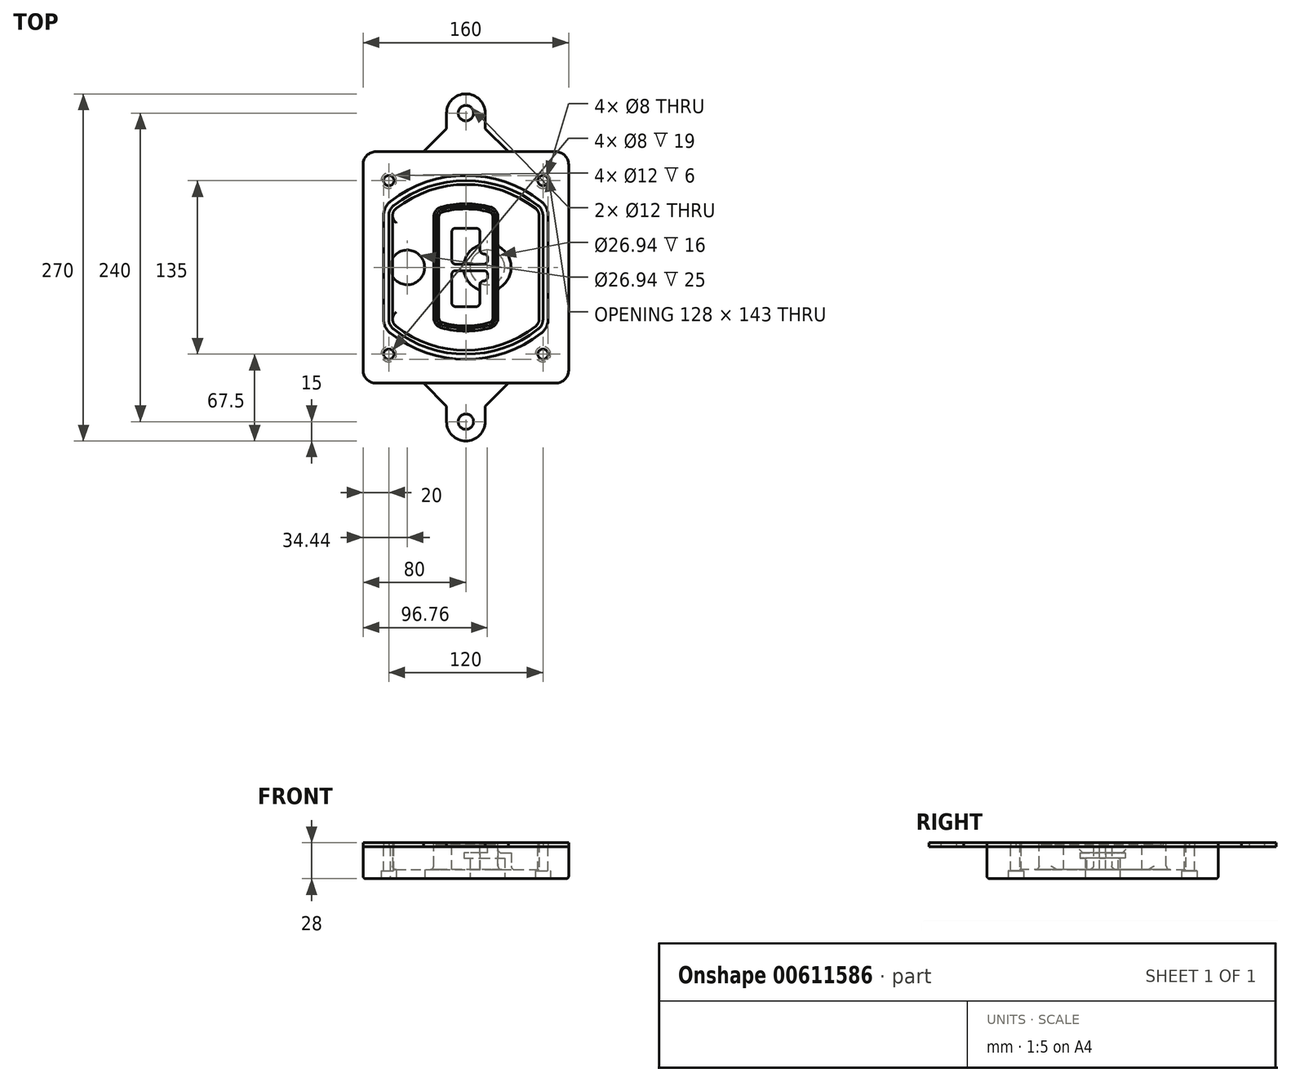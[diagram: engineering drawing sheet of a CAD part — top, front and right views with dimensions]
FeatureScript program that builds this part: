
annotation { "Feature Type Name" : "Feature", "Feature Type Description" : "" }
export const myFeature = defineFeature(function(context is Context, id is Id, definition is map)
    precondition{}
    {
        {
            var Q0;
            Q0=qCreatedBy(makeId("Top.planeOp"),FACE);
            var sketch = newSketch(context, id + "F0", { "sketchPlane" : qUnion([Q0])});
            skPoint(sketch, "E0.rect.middle", {"position": v(0, 0) * mm});
            skLineSegment(sketch, "E1.bottom", {"start": v(-70, -90) * mm, "end": v(70, -90) * mm});
            skLineSegment(sketch, "E1.top", {"start": v(-70, 90) * mm, "end": v(70, 90) * mm});
            skLineSegment(sketch, "E1.left", {"start": v(-80, -80) * mm, "end": v(-80, 80) * mm});
            skLineSegment(sketch, "E1.right", {"start": v(80, -80) * mm, "end": v(80, 80) * mm});
            skLineSegment(sketch, "E2", {"start": v(-80, 90) * mm, "end": v(80, -90) * mm, "construction": true});
            skLineSegment(sketch, "E3", {"start": v(80, 90) * mm, "end": v(-80, -90) * mm, "construction": true});
            skCircle(sketch, "E4", {"center": v(-60, 67.5) * mm, "radius": 4 * mm});
            skCircle(sketch, "E5", {"center": v(60, 67.5) * mm, "radius": 4 * mm});
            skCircle(sketch, "E6", {"center": v(60, -67.5) * mm, "radius": 4 * mm});
            skCircle(sketch, "E7", {"center": v(-60, -67.5) * mm, "radius": 4 * mm});
            skLineSegment(sketch, "E8", {"start": v(-60, 67.5) * mm, "end": v(60, 67.5) * mm, "construction": true});
            skLineSegment(sketch, "E9", {"start": v(60, 67.5) * mm, "end": v(60, -67.5) * mm, "construction": true});
            skLineSegment(sketch, "E10", {"start": v(60, -67.5) * mm, "end": v(-60, -67.5) * mm, "construction": true});
            skLineSegment(sketch, "E11", {"start": v(-60, -67.5) * mm, "end": v(-60, 67.5) * mm, "construction": true});
            skLineSegment(sketch, "E12", {"start": v(-60, 40.3) * mm, "end": v(-60, -40.3) * mm});
            skLineSegment(sketch, "E13", {"start": v(60, 40.3) * mm, "end": v(60, -40.3) * mm});
            skArc(sketch, "E14", {"start": v(56.15, 48.18) * mm, "mid": v(0, 67.5) * mm, "end": v(-56.15, 48.18) * mm});
            skArc(sketch, "E15", {"start": v(-56.15, -48.18) * mm, "mid": v(0, -67.5) * mm, "end": v(56.15, -48.18) * mm});
            skLineSegment(sketch, "E16", {"start": v(-60, 0) * mm, "end": v(60, 0) * mm, "construction": true});
            skPoint(sketch, "E17.visualSharp", {"position": v(-60, -45) * mm});
            skArc(sketch, "E17.filletArc", {"start": v(-60, -40.3) * mm, "mid": v(-58.99, -44.68) * mm, "end": v(-56.15, -48.18) * mm});
            skPoint(sketch, "E18.visualSharp", {"position": v(-60, 45) * mm});
            skArc(sketch, "E18.filletArc", {"start": v(-56.15, 48.18) * mm, "mid": v(-58.99, 44.68) * mm, "end": v(-60, 40.3) * mm});
            skPoint(sketch, "E19.visualSharp", {"position": v(60, 45) * mm});
            skArc(sketch, "E19.filletArc", {"start": v(60, 40.3) * mm, "mid": v(58.99, 44.68) * mm, "end": v(56.15, 48.18) * mm});
            skPoint(sketch, "E20.visualSharp", {"position": v(60, -45) * mm});
            skArc(sketch, "E20.filletArc", {"start": v(56.15, -48.18) * mm, "mid": v(58.99, -44.68) * mm, "end": v(60, -40.3) * mm});
            skPoint(sketch, "E21.visualSharp", {"position": v(-80, 90) * mm});
            skArc(sketch, "E21.filletArc", {"start": v(-70, 90) * mm, "mid": v(-77.07, 87.07) * mm, "end": v(-80, 80) * mm});
            skPoint(sketch, "E22.visualSharp", {"position": v(80, 90) * mm});
            skArc(sketch, "E22.filletArc", {"start": v(80, 80) * mm, "mid": v(77.07, 87.07) * mm, "end": v(70, 90) * mm});
            skPoint(sketch, "E23.visualSharp", {"position": v(80, -90) * mm});
            skArc(sketch, "E23.filletArc", {"start": v(70, -90) * mm, "mid": v(77.07, -87.07) * mm, "end": v(80, -80) * mm});
            skPoint(sketch, "E24.visualSharp", {"position": v(-80, -90) * mm});
            skArc(sketch, "E24.filletArc", {"start": v(-80, -80) * mm, "mid": v(-77.07, -87.07) * mm, "end": v(-70, -90) * mm});
            skArc(sketch, "E25.0", {"start": v(57, 40.3) * mm, "mid": v(56.3, 43.36) * mm, "end": v(54.3, 45.81) * mm});
            skLineSegment(sketch, "E25.1", {"start": v(57, 40.3) * mm, "end": v(57, -40.3) * mm});
            skArc(sketch, "E25.2", {"start": v(54.3, -45.81) * mm, "mid": v(56.3, -43.36) * mm, "end": v(57, -40.3) * mm});
            skArc(sketch, "E25.3", {"start": v(-54.3, -45.81) * mm, "mid": v(0, -64.5) * mm, "end": v(54.3, -45.81) * mm});
            skArc(sketch, "E25.4", {"start": v(-57, -40.3) * mm, "mid": v(-56.3, -43.36) * mm, "end": v(-54.3, -45.81) * mm});
            skArc(sketch, "E25.5", {"start": v(54.3, 45.81) * mm, "mid": v(0, 64.5) * mm, "end": v(-54.3, 45.81) * mm});
            skLineSegment(sketch, "E25.6", {"start": v(-57, 40.3) * mm, "end": v(-57, -40.3) * mm});
            skArc(sketch, "E25.7", {"start": v(-54.3, 45.81) * mm, "mid": v(-56.3, 43.36) * mm, "end": v(-57, 40.3) * mm});
            skArc(sketch, "E26.0", {"start": v(-58.62, 51.33) * mm, "mid": v(-62.58, 46.43) * mm, "end": v(-64, 40.3) * mm});
            skArc(sketch, "E26.1", {"start": v(58.62, 51.33) * mm, "mid": v(0, 71.5) * mm, "end": v(-58.62, 51.33) * mm});
            skArc(sketch, "E26.2", {"start": v(64, 40.3) * mm, "mid": v(62.58, 46.43) * mm, "end": v(58.62, 51.33) * mm});
            skLineSegment(sketch, "E26.3", {"start": v(64, 40.3) * mm, "end": v(64, -40.3) * mm});
            skArc(sketch, "E26.4", {"start": v(58.62, -51.33) * mm, "mid": v(62.58, -46.43) * mm, "end": v(64, -40.3) * mm});
            skLineSegment(sketch, "E26.5", {"start": v(-64, 40.3) * mm, "end": v(-64, -40.3) * mm});
            skArc(sketch, "E26.6", {"start": v(-58.62, -51.33) * mm, "mid": v(0, -71.5) * mm, "end": v(58.62, -51.33) * mm});
            skArc(sketch, "E26.7", {"start": v(-64, -40.3) * mm, "mid": v(-62.58, -46.43) * mm, "end": v(-58.62, -51.33) * mm});
            skSolve(sketch);
        }
        {
            var Q0;
            Q0=makeQuery(id+"F0.imprint","IMPRINT",FACE,{"disambiguationData":[TD([[makeQuery(id+"F0.imprint","IMPRINT",EDGE,{"derivedFrom":sQuery(id+"F0.wireOp",EDGE,"E1.bottom")}),1.0]])]});
            var Q1;
            Q1=makeQuery(id+"F0.imprint","IMPRINT",FACE,{"disambiguationData":[TD([[makeQuery(id+"F0.imprint","IMPRINT",EDGE,{"derivedFrom":sQuery(id+"F0.wireOp",EDGE,"E12")}),1.0]])]});
            var Q2;
            Q2=makeQuery(id+"F0.imprint","IMPRINT",FACE,{"disambiguationData":[TD([[makeQuery(id+"F0.imprint","IMPRINT",EDGE,{"derivedFrom":sQuery(id+"F0.wireOp",EDGE,"E25.0")}),1.0]])]});
            var Q3;
            Q3=makeQuery(id+"F0.imprint","IMPRINT",FACE,{"disambiguationData":[TD([[makeQuery(id+"F0.imprint","IMPRINT",EDGE,{"derivedFrom":sQuery(id+"F0.wireOp",EDGE,"E12")}),-1.0]])]});
            extrude(context, id + "F1", {"entities" : qUnion([Q0, Q1, Q2, Q3]), "oppositeDirection" : true, "depth" : 25 * mm});
        }
        {
            var Q0;
            Q0=makeQuery(id+"F0.imprint","IMPRINT",FACE,{"disambiguationData":[TD([[makeQuery(id+"F0.imprint","IMPRINT",EDGE,{"derivedFrom":sQuery(id+"F0.wireOp",EDGE,"E12")}),1.0]])]});
            extrude(context, id + "F2", {"entities" : qUnion([Q0]), "operationType" : NewBodyOperationType.ADD, "depth" : 3 * mm});
        }
        {
            var Q0;
            Q0=makeQuery(id+"F0.imprint","IMPRINT",FACE,{"disambiguationData":[TD([[makeQuery(id+"F0.imprint","IMPRINT",EDGE,{"derivedFrom":sQuery(id+"F0.wireOp",EDGE,"E25.0")}),1.0]])]});
            extrude(context, id + "F3", {"entities" : qUnion([Q0]), "operationType" : NewBodyOperationType.REMOVE, "oppositeDirection" : true, "depth" : 18 * mm});
        }
        {
            var Q0;
            Q0=makeQuery(id+"F2.opExtrude","CAP_FACE",FACE,{"disambiguationData":[OSD([sQuery(id+"F0.wireOp",EDGE,"E12"),sQuery(id+"F0.wireOp",EDGE,"E13"),sQuery(id+"F0.wireOp",EDGE,"E14"),sQuery(id+"F0.wireOp",EDGE,"E15"),sQuery(id+"F0.wireOp",EDGE,"E17.filletArc"),sQuery(id+"F0.wireOp",EDGE,"E18.filletArc"),sQuery(id+"F0.wireOp",EDGE,"E19.filletArc"),sQuery(id+"F0.wireOp",EDGE,"E20.filletArc"),sQuery(id+"F0.wireOp",EDGE,"E25.0"),sQuery(id+"F0.wireOp",EDGE,"E25.1"),sQuery(id+"F0.wireOp",EDGE,"E25.2"),sQuery(id+"F0.wireOp",EDGE,"E25.3"),sQuery(id+"F0.wireOp",EDGE,"E25.4"),sQuery(id+"F0.wireOp",EDGE,"E25.5"),sQuery(id+"F0.wireOp",EDGE,"E25.6"),sQuery(id+"F0.wireOp",EDGE,"E25.7")])],"isStart":false});
            var sketch = newSketch(context, id + "F4", { "sketchPlane" : qUnion([Q0])});
            skArc(sketch, "E27.0", {"start": v(-19.08, -46.97) * mm, "mid": v(0, -49.5) * mm, "end": v(19.08, -46.97) * mm});
            skArc(sketch, "E28.0", {"start": v(19.08, 46.97) * mm, "mid": v(0, 49.5) * mm, "end": v(-19.08, 46.97) * mm});
            skLineSegment(sketch, "E29", {"start": v(-25, 39.25) * mm, "end": v(-25, -39.25) * mm});
            skLineSegment(sketch, "E30", {"start": v(25, 39.25) * mm, "end": v(25, -39.25) * mm});
            skLineSegment(sketch, "E31", {"start": v(-25, 45.1) * mm, "end": v(25, 45.1) * mm, "construction": true});
            skLineSegment(sketch, "E32", {"start": v(-25, -45.1) * mm, "end": v(25, -45.1) * mm, "construction": true});
            skPoint(sketch, "E33.visualSharp", {"position": v(-25, 45.1) * mm});
            skArc(sketch, "E33.filletArc", {"start": v(-19.08, 46.97) * mm, "mid": v(-23.35, 44.11) * mm, "end": v(-25, 39.25) * mm});
            skPoint(sketch, "E34.visualSharp", {"position": v(25, 45.1) * mm});
            skArc(sketch, "E34.filletArc", {"start": v(25, 39.25) * mm, "mid": v(23.35, 44.11) * mm, "end": v(19.08, 46.97) * mm});
            skPoint(sketch, "E35.visualSharp", {"position": v(25, -45.1) * mm});
            skArc(sketch, "E35.filletArc", {"start": v(19.08, -46.97) * mm, "mid": v(23.35, -44.11) * mm, "end": v(25, -39.25) * mm});
            skPoint(sketch, "E36.visualSharp", {"position": v(-25, -45.1) * mm});
            skArc(sketch, "E36.filletArc", {"start": v(-25, -39.25) * mm, "mid": v(-23.35, -44.11) * mm, "end": v(-19.08, -46.97) * mm});
            skArc(sketch, "E37.0", {"start": v(54.3, 45.81) * mm, "mid": v(0, 64.5) * mm, "end": v(-54.3, 45.81) * mm});
            skArc(sketch, "E37.1", {"start": v(-54.3, 45.81) * mm, "mid": v(-56.3, 43.36) * mm, "end": v(-57, 40.3) * mm});
            skLineSegment(sketch, "E37.2", {"start": v(-57, 40.3) * mm, "end": v(-57, -40.3) * mm});
            skArc(sketch, "E37.3", {"start": v(-57, -40.3) * mm, "mid": v(-56.3, -43.36) * mm, "end": v(-54.3, -45.81) * mm});
            skArc(sketch, "E37.4", {"start": v(-54.3, -45.81) * mm, "mid": v(0, -64.5) * mm, "end": v(54.3, -45.81) * mm});
            skArc(sketch, "E37.5", {"start": v(54.3, -45.81) * mm, "mid": v(56.3, -43.36) * mm, "end": v(57, -40.3) * mm});
            skLineSegment(sketch, "E37.6", {"start": v(57, 40.3) * mm, "end": v(57, -40.3) * mm});
            skArc(sketch, "E37.7", {"start": v(57, 40.3) * mm, "mid": v(56.3, 43.36) * mm, "end": v(54.3, 45.81) * mm});
            skLineSegment(sketch, "E38.0", {"start": v(23, 39.25) * mm, "end": v(23, -39.25) * mm});
            skArc(sketch, "E38.1", {"start": v(18.56, -45.04) * mm, "mid": v(21.76, -42.9) * mm, "end": v(23, -39.25) * mm});
            skArc(sketch, "E38.2", {"start": v(-18.56, -45.04) * mm, "mid": v(0, -47.5) * mm, "end": v(18.56, -45.04) * mm});
            skArc(sketch, "E38.3", {"start": v(-23, -39.25) * mm, "mid": v(-21.76, -42.9) * mm, "end": v(-18.56, -45.04) * mm});
            skLineSegment(sketch, "E38.4", {"start": v(-23, 39.25) * mm, "end": v(-23, -39.25) * mm});
            skArc(sketch, "E38.5", {"start": v(23, 39.25) * mm, "mid": v(21.76, 42.9) * mm, "end": v(18.56, 45.04) * mm});
            skArc(sketch, "E38.6", {"start": v(-18.56, 45.04) * mm, "mid": v(-21.76, 42.9) * mm, "end": v(-23, 39.25) * mm});
            skArc(sketch, "E38.7", {"start": v(18.56, 45.04) * mm, "mid": v(0, 47.5) * mm, "end": v(-18.56, 45.04) * mm});
            skArc(sketch, "E39.0", {"start": v(21, 39.25) * mm, "mid": v(20.18, 41.68) * mm, "end": v(18.04, 43.1) * mm});
            skLineSegment(sketch, "E39.1", {"start": v(21, 39.25) * mm, "end": v(21, -39.25) * mm});
            skArc(sketch, "E39.2", {"start": v(18.04, -43.1) * mm, "mid": v(20.18, -41.68) * mm, "end": v(21, -39.25) * mm});
            skArc(sketch, "E39.3", {"start": v(-18.04, -43.1) * mm, "mid": v(0, -45.5) * mm, "end": v(18.04, -43.1) * mm});
            skArc(sketch, "E39.4", {"start": v(-21, -39.25) * mm, "mid": v(-20.18, -41.68) * mm, "end": v(-18.04, -43.1) * mm});
            skArc(sketch, "E39.5", {"start": v(18.04, 43.1) * mm, "mid": v(0, 45.5) * mm, "end": v(-18.04, 43.1) * mm});
            skLineSegment(sketch, "E39.6", {"start": v(-21, 39.25) * mm, "end": v(-21, -39.25) * mm});
            skArc(sketch, "E39.7", {"start": v(-18.04, 43.1) * mm, "mid": v(-20.18, 41.68) * mm, "end": v(-21, 39.25) * mm});
            skLineSegment(sketch, "E40", {"start": v(-25, 0) * mm, "end": v(25, 0) * mm, "construction": true});
            skLineSegment(sketch, "E41", {"start": v(-11, 5.5) * mm, "end": v(-11, 27.5) * mm});
            skLineSegment(sketch, "E42", {"start": v(-8, 30.5) * mm, "end": v(8, 30.5) * mm});
            skLineSegment(sketch, "E43", {"start": v(11, 27.5) * mm, "end": v(11, 13.5) * mm});
            skLineSegment(sketch, "E44", {"start": v(14, 10.5) * mm, "end": v(14, 10.5) * mm});
            skLineSegment(sketch, "E45", {"start": v(17, 7.5) * mm, "end": v(17, 5.5) * mm});
            skLineSegment(sketch, "E46", {"start": v(14, 2.5) * mm, "end": v(-8, 2.5) * mm});
            skPoint(sketch, "E47.visualSharp", {"position": v(-11, 30.5) * mm});
            skArc(sketch, "E47.filletArc", {"start": v(-8, 30.5) * mm, "mid": v(-10.12, 29.62) * mm, "end": v(-11, 27.5) * mm});
            skPoint(sketch, "E48.visualSharp", {"position": v(11, 30.5) * mm});
            skArc(sketch, "E48.filletArc", {"start": v(11, 27.5) * mm, "mid": v(10.12, 29.62) * mm, "end": v(8, 30.5) * mm});
            skPoint(sketch, "E49.visualSharp", {"position": v(11, 10.5) * mm});
            skArc(sketch, "E49.filletArc", {"start": v(11, 13.5) * mm, "mid": v(11.88, 11.38) * mm, "end": v(14, 10.5) * mm});
            skPoint(sketch, "E50.visualSharp", {"position": v(17, 10.5) * mm});
            skArc(sketch, "E50.filletArc", {"start": v(17, 7.5) * mm, "mid": v(16.12, 9.62) * mm, "end": v(14, 10.5) * mm});
            skPoint(sketch, "E51.visualSharp", {"position": v(17, 2.5) * mm});
            skArc(sketch, "E51.filletArc", {"start": v(14, 2.5) * mm, "mid": v(16.12, 3.38) * mm, "end": v(17, 5.5) * mm});
            skPoint(sketch, "E52.visualSharp", {"position": v(-11, 2.5) * mm});
            skArc(sketch, "E52.filletArc", {"start": v(-11, 5.5) * mm, "mid": v(-10.12, 3.38) * mm, "end": v(-8, 2.5) * mm});
            skLineSegment(sketch, "E53.0.MirrorCS", {"start": v(14, -2.5) * mm, "end": v(-8, -2.5) * mm});
            skArc(sketch, "E54.0.MirrorCS", {"start": v(-11, -5.5) * mm, "mid": v(-10.12, -3.38) * mm, "end": v(-8, -2.5) * mm});
            skLineSegment(sketch, "E55.0.MirrorCS", {"start": v(-11, -5.5) * mm, "end": v(-11, -27.5) * mm});
            skArc(sketch, "E56.0.MirrorCS", {"start": v(-8, -30.5) * mm, "mid": v(-10.12, -29.62) * mm, "end": v(-11, -27.5) * mm});
            skLineSegment(sketch, "E57.0.MirrorCS", {"start": v(-8, -30.5) * mm, "end": v(8, -30.5) * mm});
            skArc(sketch, "E58.0.MirrorCS", {"start": v(11, -27.5) * mm, "mid": v(10.12, -29.62) * mm, "end": v(8, -30.5) * mm});
            skLineSegment(sketch, "E59.0.MirrorCS", {"start": v(11, -27.5) * mm, "end": v(11, -13.5) * mm});
            skArc(sketch, "E60.0.MirrorCS", {"start": v(11, -13.5) * mm, "mid": v(11.88, -11.38) * mm, "end": v(14, -10.5) * mm});
            skArc(sketch, "E61.0.MirrorCS", {"start": v(17, -7.5) * mm, "mid": v(16.12, -9.62) * mm, "end": v(14, -10.5) * mm});
            skLineSegment(sketch, "E62.0.MirrorCS", {"start": v(17, -7.5) * mm, "end": v(17, -5.5) * mm});
            skArc(sketch, "E63.0.MirrorCS", {"start": v(14, -2.5) * mm, "mid": v(16.12, -3.38) * mm, "end": v(17, -5.5) * mm});
            skSolve(sketch);
        }
        {
            var Q0;
            Q0=makeQuery(id+"F4.imprint","IMPRINT",FACE,{"disambiguationData":[TD([[makeQuery(id+"F4.imprint","IMPRINT",EDGE,{"derivedFrom":sQuery(id+"F4.wireOp",EDGE,"E27.0")}),1.0]])]});
            var Q1;
            Q1=makeQuery(id+"F4.imprint","IMPRINT",FACE,{"disambiguationData":[TD([[makeQuery(id+"F4.imprint","IMPRINT",EDGE,{"derivedFrom":sQuery(id+"F4.wireOp",EDGE,"E38.0")}),-1.0]])]});
            var Q2;
            Q2=makeQuery(id+"F4.imprint","IMPRINT",FACE,{"disambiguationData":[TD([[makeQuery(id+"F4.imprint","IMPRINT",EDGE,{"derivedFrom":sQuery(id+"F4.wireOp",EDGE,"E39.0")}),1.0]])]});
            extrude(context, id + "F5", {"entities" : qUnion([Q0, Q1, Q2]), "operationType" : NewBodyOperationType.ADD, "endBound" : BoundingType.UP_TO_NEXT, "oppositeDirection" : true, "depth" : 25 * mm});
        }
        {
            var Q0;
            Q0=makeQuery(id+"F4.imprint","IMPRINT",FACE,{"disambiguationData":[TD([[makeQuery(id+"F4.imprint","IMPRINT",EDGE,{"derivedFrom":sQuery(id+"F4.wireOp",EDGE,"E38.0")}),-1.0]])]});
            extrude(context, id + "F6", {"entities" : qUnion([Q0]), "operationType" : NewBodyOperationType.REMOVE, "oppositeDirection" : true, "depth" : 2 * mm});
        }
        {
            var Q0;
            Q0=makeQuery(id+"F1.opExtrude","CAP_FACE",FACE,{"disambiguationData":[OSD([sQuery(id+"F0.wireOp",EDGE,"E1.bottom"),sQuery(id+"F0.wireOp",EDGE,"E1.top"),sQuery(id+"F0.wireOp",EDGE,"E1.left"),sQuery(id+"F0.wireOp",EDGE,"E1.right"),sQuery(id+"F0.wireOp",EDGE,"E4"),sQuery(id+"F0.wireOp",EDGE,"E5"),sQuery(id+"F0.wireOp",EDGE,"E6"),sQuery(id+"F0.wireOp",EDGE,"E7"),sQuery(id+"F0.wireOp",EDGE,"E21.filletArc"),sQuery(id+"F0.wireOp",EDGE,"E22.filletArc"),sQuery(id+"F0.wireOp",EDGE,"E23.filletArc"),sQuery(id+"F0.wireOp",EDGE,"E24.filletArc")])],"isStart":false});
            var sketch = newSketch(context, id + "F7", { "sketchPlane" : qUnion([Q0])});
            skCircle(sketch, "E64", {"center": v(16.76, 0) * mm, "radius": 13.47 * mm});
            skCircle(sketch, "E65", {"center": v(-45.56, 0) * mm, "radius": 13.47 * mm});
            skLineSegment(sketch, "E66", {"start": v(80, 0) * mm, "end": v(-80, 0) * mm});
            skCircle(sketch, "E67", {"center": v(16.76, 0) * mm, "radius": 18.47 * mm});
            skCircle(sketch, "E68", {"center": v(60, -67.5) * mm, "radius": 6 * mm});
            skCircle(sketch, "E69", {"center": v(-60, -67.5) * mm, "radius": 6 * mm});
            skCircle(sketch, "E70", {"center": v(-60, 67.5) * mm, "radius": 6 * mm});
            skCircle(sketch, "E71", {"center": v(60, 67.5) * mm, "radius": 6 * mm});
            skSolve(sketch);
        }
        {
            var Q0;
            {var subQ1=sQuery(id+"F7.wireOp",EDGE,"E66");var subQ4=sQuery(id+"F7.wireOp",EDGE,"E64");var subQ6=makeQuery(id+"F7.imprint","INTERSECT",VERTEX,{"disambiguationData":[OD(0.0)],"derivedFrom":[subQ4,subQ1]});Q0=makeQuery(id+"F7.imprint","IMPRINT",FACE,{"disambiguationData":[TD([[makeQuery(id+"F7.imprint","IMPRINT",EDGE,{"disambiguationData":[TD([[subQ6,-1.0]])],"derivedFrom":subQ4}),-1.0]])]});}
            var Q1;
            {var subQ0=sQuery(id+"F7.wireOp",EDGE,"E66");var subQ1=sQuery(id+"F7.wireOp",EDGE,"E64");var subQ3=makeQuery(id+"F7.imprint","INTERSECT",VERTEX,{"disambiguationData":[OD(0.0)],"derivedFrom":[subQ1,subQ0]});Q1=makeQuery(id+"F7.imprint","IMPRINT",FACE,{"disambiguationData":[TD([[makeQuery(id+"F7.imprint","IMPRINT",EDGE,{"disambiguationData":[TD([[subQ3,-1.0]])],"derivedFrom":subQ1}),1.0]])]});}
            var Q2;
            {var subQ0=sQuery(id+"F7.wireOp",EDGE,"E66");var subQ1=sQuery(id+"F7.wireOp",EDGE,"E64");var subQ3=makeQuery(id+"F7.imprint","INTERSECT",VERTEX,{"disambiguationData":[OD(0.0)],"derivedFrom":[subQ1,subQ0]});Q2=makeQuery(id+"F7.imprint","IMPRINT",FACE,{"disambiguationData":[TD([[makeQuery(id+"F7.imprint","IMPRINT",EDGE,{"disambiguationData":[TD([[subQ3,1.0]])],"derivedFrom":subQ1}),1.0]])]});}
            var Q3;
            {var subQ1=sQuery(id+"F7.wireOp",EDGE,"E66");var subQ4=sQuery(id+"F7.wireOp",EDGE,"E64");var subQ6=makeQuery(id+"F7.imprint","INTERSECT",VERTEX,{"disambiguationData":[OD(0.0)],"derivedFrom":[subQ4,subQ1]});Q3=makeQuery(id+"F7.imprint","IMPRINT",FACE,{"disambiguationData":[TD([[makeQuery(id+"F7.imprint","IMPRINT",EDGE,{"disambiguationData":[TD([[subQ6,1.0]])],"derivedFrom":subQ4}),-1.0]])]});}
            extrude(context, id + "F8", {"entities" : qUnion([Q0, Q1, Q2, Q3]), "operationType" : NewBodyOperationType.ADD, "oppositeDirection" : true, "depth" : 20 * mm});
        }
        {
            var Q0;
            {var subQ0=sQuery(id+"F7.wireOp",EDGE,"E66");var subQ1=sQuery(id+"F7.wireOp",EDGE,"E64");var subQ3=makeQuery(id+"F7.imprint","INTERSECT",VERTEX,{"disambiguationData":[OD(0.0)],"derivedFrom":[subQ1,subQ0]});Q0=makeQuery(id+"F7.imprint","IMPRINT",FACE,{"disambiguationData":[TD([[makeQuery(id+"F7.imprint","IMPRINT",EDGE,{"disambiguationData":[TD([[subQ3,-1.0]])],"derivedFrom":subQ1}),1.0]])]});}
            var Q1;
            {var subQ0=sQuery(id+"F7.wireOp",EDGE,"E66");var subQ1=sQuery(id+"F7.wireOp",EDGE,"E64");var subQ3=makeQuery(id+"F7.imprint","INTERSECT",VERTEX,{"disambiguationData":[OD(0.0)],"derivedFrom":[subQ1,subQ0]});Q1=makeQuery(id+"F7.imprint","IMPRINT",FACE,{"disambiguationData":[TD([[makeQuery(id+"F7.imprint","IMPRINT",EDGE,{"disambiguationData":[TD([[subQ3,1.0]])],"derivedFrom":subQ1}),1.0]])]});}
            extrude(context, id + "F9", {"entities" : qUnion([Q0, Q1]), "operationType" : NewBodyOperationType.REMOVE, "oppositeDirection" : true, "depth" : 16 * mm});
        }
        {
            var Q0;
            {var subQ0=sQuery(id+"F7.wireOp",EDGE,"E66");var subQ1=sQuery(id+"F7.wireOp",EDGE,"E65");var subQ3=makeQuery(id+"F7.imprint","INTERSECT",VERTEX,{"disambiguationData":[OD(0.0)],"derivedFrom":[subQ1,subQ0]});Q0=makeQuery(id+"F7.imprint","IMPRINT",FACE,{"disambiguationData":[TD([[makeQuery(id+"F7.imprint","IMPRINT",EDGE,{"disambiguationData":[TD([[subQ3,-1.0]])],"derivedFrom":subQ1}),1.0]])]});}
            var Q1;
            {var subQ0=sQuery(id+"F7.wireOp",EDGE,"E66");var subQ1=sQuery(id+"F7.wireOp",EDGE,"E65");var subQ3=makeQuery(id+"F7.imprint","INTERSECT",VERTEX,{"disambiguationData":[OD(0.0)],"derivedFrom":[subQ1,subQ0]});Q1=makeQuery(id+"F7.imprint","IMPRINT",FACE,{"disambiguationData":[TD([[makeQuery(id+"F7.imprint","IMPRINT",EDGE,{"disambiguationData":[TD([[subQ3,1.0]])],"derivedFrom":subQ1}),1.0]])]});}
            extrude(context, id + "F10", {"entities" : qUnion([Q0, Q1]), "operationType" : NewBodyOperationType.REMOVE, "oppositeDirection" : true, "depth" : 25 * mm});
        }
        {
            var Q0;
            Q0=makeQuery(id+"F7.imprint","IMPRINT",FACE,{"disambiguationData":[TD([[makeQuery(id+"F7.imprint","IMPRINT",EDGE,{"derivedFrom":sQuery(id+"F7.wireOp",EDGE,"E68")}),1.0]])]});
            var Q1;
            Q1=makeQuery(id+"F7.imprint","IMPRINT",FACE,{"disambiguationData":[TD([[makeQuery(id+"F7.imprint","IMPRINT",EDGE,{"derivedFrom":makeQuery(id+"F1.opExtrude","CAP_EDGE",EDGE,{"disambiguationData":[OSD([sQuery(id+"F0.wireOp",EDGE,"E5")])],"isStart":false})}),-1.0]])]});
            var Q2;
            Q2=makeQuery(id+"F7.imprint","IMPRINT",FACE,{"disambiguationData":[TD([[makeQuery(id+"F7.imprint","IMPRINT",EDGE,{"derivedFrom":sQuery(id+"F7.wireOp",EDGE,"E69")}),1.0]])]});
            var Q3;
            Q3=makeQuery(id+"F7.imprint","IMPRINT",FACE,{"disambiguationData":[TD([[makeQuery(id+"F7.imprint","IMPRINT",EDGE,{"derivedFrom":makeQuery(id+"F1.opExtrude","CAP_EDGE",EDGE,{"disambiguationData":[OSD([sQuery(id+"F0.wireOp",EDGE,"E4")])],"isStart":false})}),-1.0]])]});
            var Q4;
            Q4=makeQuery(id+"F7.imprint","IMPRINT",FACE,{"disambiguationData":[TD([[makeQuery(id+"F7.imprint","IMPRINT",EDGE,{"derivedFrom":sQuery(id+"F7.wireOp",EDGE,"E70")}),1.0]])]});
            var Q5;
            Q5=makeQuery(id+"F7.imprint","IMPRINT",FACE,{"disambiguationData":[TD([[makeQuery(id+"F7.imprint","IMPRINT",EDGE,{"derivedFrom":makeQuery(id+"F1.opExtrude","CAP_EDGE",EDGE,{"disambiguationData":[OSD([sQuery(id+"F0.wireOp",EDGE,"E7")])],"isStart":false})}),-1.0]])]});
            var Q6;
            Q6=makeQuery(id+"F7.imprint","IMPRINT",FACE,{"disambiguationData":[TD([[makeQuery(id+"F7.imprint","IMPRINT",EDGE,{"derivedFrom":sQuery(id+"F7.wireOp",EDGE,"E71")}),1.0]])]});
            var Q7;
            Q7=makeQuery(id+"F7.imprint","IMPRINT",FACE,{"disambiguationData":[TD([[makeQuery(id+"F7.imprint","IMPRINT",EDGE,{"derivedFrom":makeQuery(id+"F1.opExtrude","CAP_EDGE",EDGE,{"disambiguationData":[OSD([sQuery(id+"F0.wireOp",EDGE,"E6")])],"isStart":false})}),-1.0]])]});
            extrude(context, id + "F11", {"entities" : qUnion([Q0, Q1, Q2, Q3, Q4, Q5, Q6, Q7]), "operationType" : NewBodyOperationType.REMOVE, "oppositeDirection" : true, "depth" : 6 * mm});
        }
        {
            var Q0;
            Q0=makeQuery(id+"F9.boolean.opBoolean","COPY",FACE,{"derivedFrom":makeQuery(id+"F9.opExtrude","CAP_FACE",FACE,{"disambiguationData":[OSD([sQuery(id+"F7.wireOp",EDGE,"E64")])],"isStart":false})});
            var sketch = newSketch(context, id + "F12", { "sketchPlane" : qUnion([Q0])});
            skArc(sketch, "E72.0", {"start": v(11, 17.55) * mm, "mid": v(2.57, 11.82) * mm, "end": v(-1.54, 2.5) * mm});
            skArc(sketch, "E72.1", {"start": v(-1.54, -2.5) * mm, "mid": v(2.57, -11.82) * mm, "end": v(11, -17.55) * mm});
            skLineSegment(sketch, "E73", {"start": v(-1.54, -2.5) * mm, "end": v(14, -2.5) * mm});
            skLineSegment(sketch, "E74.0", {"start": v(14, 2.5) * mm, "end": v(-1.54, 2.5) * mm});
            skArc(sketch, "E74.1", {"start": v(14, 2.5) * mm, "mid": v(16.12, 3.38) * mm, "end": v(17, 5.5) * mm});
            skLineSegment(sketch, "E74.2", {"start": v(17, 7.5) * mm, "end": v(17, 5.5) * mm});
            skArc(sketch, "E74.3", {"start": v(17, 7.5) * mm, "mid": v(16.12, 9.62) * mm, "end": v(14, 10.5) * mm});
            skArc(sketch, "E74.4", {"start": v(11, 13.5) * mm, "mid": v(11.88, 11.38) * mm, "end": v(14, 10.5) * mm});
            skLineSegment(sketch, "E74.5", {"start": v(11, 17.55) * mm, "end": v(11, 13.5) * mm});
            skLineSegment(sketch, "E74.7", {"start": v(14, -2.5) * mm, "end": v(-1.54, -2.5) * mm});
            skArc(sketch, "E74.8", {"start": v(14, -2.5) * mm, "mid": v(16.12, -3.38) * mm, "end": v(17, -5.5) * mm});
            skLineSegment(sketch, "E74.9", {"start": v(17, -7.5) * mm, "end": v(17, -5.5) * mm});
            skArc(sketch, "E74.10", {"start": v(17, -7.5) * mm, "mid": v(16.12, -9.62) * mm, "end": v(14, -10.5) * mm});
            skArc(sketch, "E74.11", {"start": v(11, -13.5) * mm, "mid": v(11.88, -11.38) * mm, "end": v(14, -10.5) * mm});
            skLineSegment(sketch, "E74.12", {"start": v(11, -17.55) * mm, "end": v(11, -13.5) * mm});
            skPoint(sketch, "E75.orphan", {"position": v(11, -27.5) * mm});
            skPoint(sketch, "E76.orphan", {"position": v(-8, -2.5) * mm});
            skPoint(sketch, "E77.orphan", {"position": v(-8, 2.5) * mm});
            skPoint(sketch, "E78.orphan", {"position": v(11, 27.5) * mm});
            skSolve(sketch);
        }
        {
            var Q0;
            {var subQ7=sQuery(id+"F12.wireOp",EDGE,"E72.0");var subQ14=sQuery(id+"F12.wireOp",EDGE,"E72.1");var subQ16=sQuery(id+"F12.wireOp",EDGE,"E74.1");var subQ18=sQuery(id+"F12.wireOp",EDGE,"E74.8");Q0=qUnion([makeQuery(id+"F12.imprint","IMPRINT",FACE,{"disambiguationData":[TD([[makeQuery(id+"F12.imprint","IMPRINT",EDGE,{"derivedFrom":subQ7}),1.0]])]}),makeQuery(id+"F12.imprint","IMPRINT",FACE,{"disambiguationData":[TD([[makeQuery(id+"F12.imprint","IMPRINT",EDGE,{"derivedFrom":subQ14}),1.0]])]}),makeQuery(id+"F12.imprint","IMPRINT",FACE,{"disambiguationData":[TD([[makeQuery(id+"F12.imprint","IMPRINT",EDGE,{"derivedFrom":subQ16}),1.0]])]}),makeQuery(id+"F12.imprint","IMPRINT",FACE,{"disambiguationData":[TD([[makeQuery(id+"F12.imprint","IMPRINT",EDGE,{"derivedFrom":subQ18}),-1.0]])]})]);}
            var Q1;
            Q1=makeQuery(id+"F5.boolean.opBoolean","SPLIT",FACE,{"disambiguationData":[TD([makeQuery(id+"F5.opExtrude","SWEPT_FACE",FACE,{"disambiguationData":[OSD([sQuery(id+"F4.wireOp",EDGE,"E41")])]})])],"derivedFrom":makeQuery(id+"F3.boolean.opBoolean","COPY",FACE,{"derivedFrom":makeQuery(id+"F3.opExtrude","CAP_FACE",FACE,{"disambiguationData":[OSD([sQuery(id+"F0.wireOp",EDGE,"E25.0"),sQuery(id+"F0.wireOp",EDGE,"E25.1"),sQuery(id+"F0.wireOp",EDGE,"E25.2"),sQuery(id+"F0.wireOp",EDGE,"E25.3"),sQuery(id+"F0.wireOp",EDGE,"E25.4"),sQuery(id+"F0.wireOp",EDGE,"E25.5"),sQuery(id+"F0.wireOp",EDGE,"E25.6"),sQuery(id+"F0.wireOp",EDGE,"E25.7")])],"isStart":false})})});
            extrude(context, id + "F13", {"entities" : qUnion([Q0]), "operationType" : NewBodyOperationType.REMOVE, "endBound" : BoundingType.UP_TO_SURFACE, "endBoundEntityFace" : qUnion([Q1]), "depth" : 25 * mm});
        }
        {
            var Q0;
            Q0=makeQuery(id+"F3.boolean.opBoolean","COPY",EDGE,{"derivedFrom":makeQuery(id+"F3.opExtrude","CAP_EDGE",EDGE,{"disambiguationData":[OSD([sQuery(id+"F0.wireOp",EDGE,"E25.6")])],"isStart":false})});
            var Q1;
            Q1=makeQuery(id+"F8.boolean.opBoolean","INTERSECT",EDGE,{"derivedFrom":[makeQuery(id+"F5.opExtrude","SWEPT_FACE",FACE,{"disambiguationData":[OSD([sQuery(id+"F4.wireOp",EDGE,"E30")])]}),makeQuery(id+"F8.opExtrude","CAP_FACE",FACE,{"disambiguationData":[OSD([sQuery(id+"F7.wireOp",EDGE,"E67")])],"isStart":false})]});
            var Q2;
            Q2=makeQuery(id+"F8.boolean.opBoolean","INTERSECT",EDGE,{"disambiguationData":[OD(1.0)],"derivedFrom":[makeQuery(id+"F5.opExtrude","SWEPT_FACE",FACE,{"disambiguationData":[OSD([sQuery(id+"F4.wireOp",EDGE,"E30")])]}),makeQuery(id+"F8.opExtrude","SWEPT_FACE",FACE,{"disambiguationData":[OSD([sQuery(id+"F7.wireOp",EDGE,"E67")])]})]});
            var Q3;
            {var subQ0=sQuery(id+"F4.wireOp",EDGE,"E30");Q3=makeQuery(id+"F8.boolean.opBoolean","SPLIT",EDGE,{"disambiguationData":[TD([makeQuery(id+"F5.opExtrude","SWEPT_FACE",FACE,{"disambiguationData":[OSD([sQuery(id+"F4.wireOp",EDGE,"E35.filletArc")])]})])],"derivedFrom":makeQuery(id+"F5.opExtrude","CAP_EDGE",EDGE,{"disambiguationData":[OSD([subQ0])],"isStart":false})});}
            var Q4;
            {var subQ0=sQuery(id+"F0.wireOp",EDGE,"E25.7");var subQ1=sQuery(id+"F0.wireOp",EDGE,"E25.1");var subQ2=sQuery(id+"F0.wireOp",EDGE,"E25.6");var subQ3=sQuery(id+"F0.wireOp",EDGE,"E25.5");var subQ4=sQuery(id+"F0.wireOp",EDGE,"E25.4");var subQ5=sQuery(id+"F0.wireOp",EDGE,"E25.0");var subQ6=sQuery(id+"F0.wireOp",EDGE,"E25.2");var subQ7=sQuery(id+"F0.wireOp",EDGE,"E25.3");Q4=makeQuery(id+"F8.boolean.opBoolean","INTERSECT",EDGE,{"derivedFrom":[makeQuery(id+"F5.boolean.opBoolean","SPLIT",FACE,{"disambiguationData":[TD([makeQuery(id+"F2.opExtrude","SWEPT_FACE",FACE,{"disambiguationData":[OSD([subQ5])]})])],"derivedFrom":makeQuery(id+"F3.boolean.opBoolean","COPY",FACE,{"derivedFrom":makeQuery(id+"F3.opExtrude","CAP_FACE",FACE,{"disambiguationData":[OSD([subQ5,subQ1,subQ6,subQ7,subQ4,subQ3,subQ2,subQ0])],"isStart":false})})}),makeQuery(id+"F8.opExtrude","SWEPT_FACE",FACE,{"disambiguationData":[OSD([sQuery(id+"F7.wireOp",EDGE,"E67")])]})]});}
            var Q5;
            Q5=makeQuery(id+"F8.boolean.opBoolean","INTERSECT",EDGE,{"disambiguationData":[OD(0.0)],"derivedFrom":[makeQuery(id+"F5.opExtrude","SWEPT_FACE",FACE,{"disambiguationData":[OSD([sQuery(id+"F4.wireOp",EDGE,"E30")])]}),makeQuery(id+"F8.opExtrude","SWEPT_FACE",FACE,{"disambiguationData":[OSD([sQuery(id+"F7.wireOp",EDGE,"E67")])]})]});
            fillet(context, id + "F14", {"entities" : qUnion([Q0, Q1, Q2, Q3, Q4, Q5]), "radius" : 3 * mm, "tangentPropagation" : true, "allowEdgeOverflow" : false});
        }
        {
            var Q0;
            Q0=makeQuery(id+"F1.opExtrude","CAP_EDGE",EDGE,{"disambiguationData":[OSD([sQuery(id+"F0.wireOp",EDGE,"E1.bottom")])],"isStart":false});
            fillet(context, id + "F15", {"entities" : qUnion([Q0]), "radius" : 2 * mm, "tangentPropagation" : true, "allowEdgeOverflow" : false});
        }
        {
            var Q0;
            {var subQ0=sQuery(id+"F0.wireOp",EDGE,"E21.filletArc");var subQ1=sQuery(id+"F0.wireOp",EDGE,"E7");var subQ2=sQuery(id+"F0.wireOp",EDGE,"E6");var subQ3=sQuery(id+"F0.wireOp",EDGE,"E5");var subQ4=sQuery(id+"F0.wireOp",EDGE,"E4");var subQ5=sQuery(id+"F0.wireOp",EDGE,"E22.filletArc");var subQ6=sQuery(id+"F0.wireOp",EDGE,"E1.bottom");var subQ7=sQuery(id+"F0.wireOp",EDGE,"E1.right");var subQ8=sQuery(id+"F0.wireOp",EDGE,"E1.top");var subQ9=sQuery(id+"F0.wireOp",EDGE,"E1.left");var subQ10=sQuery(id+"F0.wireOp",EDGE,"E23.filletArc");var subQ11=sQuery(id+"F0.wireOp",EDGE,"E24.filletArc");Q0=makeQuery(id+"F2.boolean.opBoolean","SPLIT",FACE,{"disambiguationData":[TD([makeQuery(id+"F1.opExtrude","SWEPT_FACE",FACE,{"disambiguationData":[OSD([subQ6])]})])],"derivedFrom":makeQuery(id+"F1.opExtrude","CAP_FACE",FACE,{"disambiguationData":[OSD([subQ6,subQ8,subQ9,subQ7,subQ4,subQ3,subQ2,subQ1,subQ0,subQ5,subQ10,subQ11])],"isStart":true})});}
            var sketch = newSketch(context, id + "F16", { "sketchPlane" : qUnion([Q0])});
            skLineSegment(sketch, "E79", {"start": v(0, 90) * mm, "end": v(0, 120) * mm, "construction": true});
            skCircle(sketch, "E80", {"center": v(0, 120) * mm, "radius": 6 * mm});
            skArc(sketch, "E81", {"start": v(15, 120) * mm, "mid": v(0, 135) * mm, "end": v(-15, 120) * mm});
            skLineSegment(sketch, "E82", {"start": v(-15, 120) * mm, "end": v(-15, 108) * mm});
            skLineSegment(sketch, "E83", {"start": v(-15, 108) * mm, "end": v(-33, 90) * mm});
            skLineSegment(sketch, "E84", {"start": v(15, 120) * mm, "end": v(15, 108) * mm});
            skLineSegment(sketch, "E85", {"start": v(15, 108) * mm, "end": v(33, 90) * mm});
            skLineSegment(sketch, "E86", {"start": v(-80, 0) * mm, "end": v(80, 0) * mm, "construction": true});
            skArc(sketch, "E87.MirrorCS", {"start": v(-15, 120) * mm, "mid": v(0, 135) * mm, "end": v(15, 120) * mm});
            skLineSegment(sketch, "E88.MirrorCS", {"start": v(80, 0) * mm, "end": v(-80, 0) * mm, "construction": true});
            skLineSegment(sketch, "E89.MirrorCS", {"start": v(15, -120) * mm, "end": v(15, -108) * mm});
            skLineSegment(sketch, "E90.MirrorCS", {"start": v(-15, -120) * mm, "end": v(-15, -108) * mm});
            skCircle(sketch, "E91.MirrorC", {"center": v(0, -120) * mm, "radius": 6 * mm});
            skLineSegment(sketch, "E92.MirrorCS", {"start": v(15, -108) * mm, "end": v(33, -90) * mm});
            skLineSegment(sketch, "E93.MirrorCS", {"start": v(-15, -108) * mm, "end": v(-33, -90) * mm});
            skArc(sketch, "E94.MirrorCS", {"start": v(15, -120) * mm, "mid": v(0, -135) * mm, "end": v(-15, -120) * mm});
            skArc(sketch, "E95.MirrorCS", {"start": v(-15, -120) * mm, "mid": v(0, -135) * mm, "end": v(15, -120) * mm});
            skLineSegment(sketch, "E96.MirrorCS", {"start": v(0, -90) * mm, "end": v(0, -120) * mm, "construction": true});
            skSolve(sketch);
        }
        {
            var Q0;
            Q0=makeQuery(id+"F16.imprint","IMPRINT",FACE,{"disambiguationData":[TD([[makeQuery(id+"F16.imprint","IMPRINT",EDGE,{"derivedFrom":sQuery(id+"F16.wireOp",EDGE,"E84")}),-1.0]])]});
            var Q1;
            Q1=makeQuery(id+"F16.imprint","IMPRINT",FACE,{"disambiguationData":[TD([[makeQuery(id+"F16.imprint","IMPRINT",EDGE,{"derivedFrom":sQuery(id+"F16.wireOp",EDGE,"E90.MirrorCS")}),-1.0]])]});
            var Q2;
            Q2=makeQuery(id+"F2.opExtrude","CAP_FACE",FACE,{"disambiguationData":[OSD([sQuery(id+"F0.wireOp",EDGE,"E12"),sQuery(id+"F0.wireOp",EDGE,"E13"),sQuery(id+"F0.wireOp",EDGE,"E14"),sQuery(id+"F0.wireOp",EDGE,"E15"),sQuery(id+"F0.wireOp",EDGE,"E17.filletArc"),sQuery(id+"F0.wireOp",EDGE,"E18.filletArc"),sQuery(id+"F0.wireOp",EDGE,"E19.filletArc"),sQuery(id+"F0.wireOp",EDGE,"E20.filletArc"),sQuery(id+"F0.wireOp",EDGE,"E25.0"),sQuery(id+"F0.wireOp",EDGE,"E25.1"),sQuery(id+"F0.wireOp",EDGE,"E25.2"),sQuery(id+"F0.wireOp",EDGE,"E25.3"),sQuery(id+"F0.wireOp",EDGE,"E25.4"),sQuery(id+"F0.wireOp",EDGE,"E25.5"),sQuery(id+"F0.wireOp",EDGE,"E25.6"),sQuery(id+"F0.wireOp",EDGE,"E25.7")])],"isStart":false});
            extrude(context, id + "F17", {"entities" : qUnion([Q0, Q1]), "endBound" : BoundingType.UP_TO_SURFACE, "depth" : 25 * mm, "endBoundEntityFace" : qUnion([Q2]), "offsetDistance" : 25 * mm});
        }
        {
            var Q0;
            Q0=makeQuery(id+"F0.imprint","IMPRINT",FACE,{"disambiguationData":[TD([[makeQuery(id+"F0.imprint","IMPRINT",EDGE,{"derivedFrom":sQuery(id+"F0.wireOp",EDGE,"E1.bottom")}),1.0]])]});
            var Q1;
            Q1=makeQuery(id+"F2.opExtrude","CAP_FACE",FACE,{"disambiguationData":[OSD([sQuery(id+"F0.wireOp",EDGE,"E12"),sQuery(id+"F0.wireOp",EDGE,"E13"),sQuery(id+"F0.wireOp",EDGE,"E14"),sQuery(id+"F0.wireOp",EDGE,"E15"),sQuery(id+"F0.wireOp",EDGE,"E17.filletArc"),sQuery(id+"F0.wireOp",EDGE,"E18.filletArc"),sQuery(id+"F0.wireOp",EDGE,"E19.filletArc"),sQuery(id+"F0.wireOp",EDGE,"E20.filletArc"),sQuery(id+"F0.wireOp",EDGE,"E25.0"),sQuery(id+"F0.wireOp",EDGE,"E25.1"),sQuery(id+"F0.wireOp",EDGE,"E25.2"),sQuery(id+"F0.wireOp",EDGE,"E25.3"),sQuery(id+"F0.wireOp",EDGE,"E25.4"),sQuery(id+"F0.wireOp",EDGE,"E25.5"),sQuery(id+"F0.wireOp",EDGE,"E25.6"),sQuery(id+"F0.wireOp",EDGE,"E25.7")])],"isStart":false});
            extrude(context, id + "F18", {"entities" : qUnion([Q0]), "endBound" : BoundingType.UP_TO_SURFACE, "depth" : 25 * mm, "endBoundEntityFace" : qUnion([Q1]), "offsetDistance" : 25 * mm});
        }
    });
